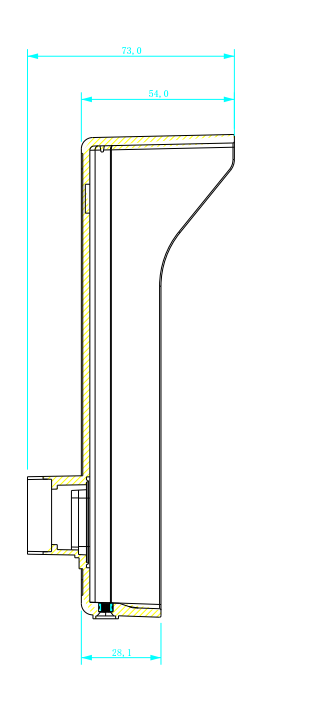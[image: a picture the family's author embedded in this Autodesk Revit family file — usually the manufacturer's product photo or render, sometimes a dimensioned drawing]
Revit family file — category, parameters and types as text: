
# Revit family: AZ-07LF
name_source: partatom
category: Устройства связи
units: mm (PartAtom-declared; Revit-internal decimal feet)

## family parameters
Всегда вертикально = Нет
На основе рабочей плоскости = Да
Общий = Да
При загрузке вырезать с полостями = Нет
Размер круглого соединителя = Использовать диаметр
Сохранять ориентацию аннотаций = Нет
Тип детали = Нормальный
Точка расчета площади = Нет

## types (1)
- AZ-07LF
    ADSK_URL документации изделия = https://cdn.bas-ip.com
    ADSK_URL страницы изделия = https://bas-ip.com
    ADSK_Версия Revit = Revit 2020
    ADSK_Единица измерения = шт
    ADSK_Завод-изготовитель = BAS-IP
    ADSK_Классификация нагрузок = Внутренний монитор индивидуальный
    ADSK_Количество фаз = 1
    ADSK_Коэффициент мощности = 0.9
    ADSK_Марка = AZ-07LF
    ADSK_Наименование = Внутренний монитор индивидуальный AZ-07LF
    ADSK_Наименование краткое = AZ-07LF
    ADSK_Напряжение = 12 В
    ADSK_Номинальная мощность = 3 Вт
    ADSK_Полная мощность = 3 В·А
    ADSK_Размер_Длина = 127 мм
    ADSK_Размер_Толщина = 27 мм
    ADSK_Размер_Ширина = 195 мм
    BIM library = https://bimlib.ru
    URL = https://www.bas-ip.ru
    Автоответчик = да
    Варианты монтажа = горизонтальный и вертикальный
    Возможность установки сторонних приложений = да
    Встроенная камера = нет
    Выберите тип скринсейвера в режиме ожидания = многокамерный просмотр в реальном времени — до 4 IP камер одновременно; Часы; Фоторамка; Просмотр тура в реальном времени — до 16 камер, время регулируется; Просмотр в реальном времени с одной IP-камеры
    Группа модели = Внутренний монитор индивидуальный
    Дополнительные разъемы = слот для карты SD (SDHC)
    Загрузка пользовательских рингтонов в формате MP3 = да
    Изготовитель = BAS-IP
    Изображение типоразмера = <Нет>
    Интерфейс = многоязычный графический и веб-интерфейс
    Количество IP-камер = до 32 камер
    Количество мелодий звонка = 9 мелодий на выбор
    Количество многоквартирных панелей = до 9 панелей
    Количество отдельных панелей = до 9 панелей
    Корпус = пластик
    Мультимедийные функции = просмотр видео, фото и аудио файлов с SD-карты
    Обновление ПО = из веб-интерфейса; С SD-карты; С сервера обновлений BAS-IP
    Описание = 7 дюймовый IP видеодомофон с настенным горизонтальным и вертикальным монтажом, возможностью управления лифтом, выводом сообщений от управляющей компании, PoE, подключением 32 камер, памятью для фото/видео и автоответчиком. ОС — Android.
    Отметка по умолчанию = 0 мм
    Питание = PoE и +12 В постоянного тока (блок питания не входит в комплект)
    Поддержка получения сообщений = да
    Поддержка сторонних виджетов = да
    Подключение дополнительных мониторов = до 8 мониторов
    Потребляемая мощность = 6 Вт, в режиме ожидания 2,5 Вт
    Размеры = 195х127х27 мм
    Разрешение экрана = 1024 х 600
    Режим «Не беспокоить» = да, настраивается по времени
    Режим ожидания = да, настраивается по времени
    Резервные фотографии, сделанные во время разговора = да
    Сетевое подключение = провод Ethernet UTP
    Сцена = да
    Тип домофона = видеодомофон, без встроенной камеры
    Тип установки = настенное крепление
    Тихий режим = да, настраивается по времени
    Управление домашней автоматикой = свет / шторы / лифт
    Функция памяти = запись фото, видео и аудио на SD-карту
    Цветовое решение = черный/серый
    Экран = 7-дюймовый IPS LCD (емкостный сенсорный экран)
